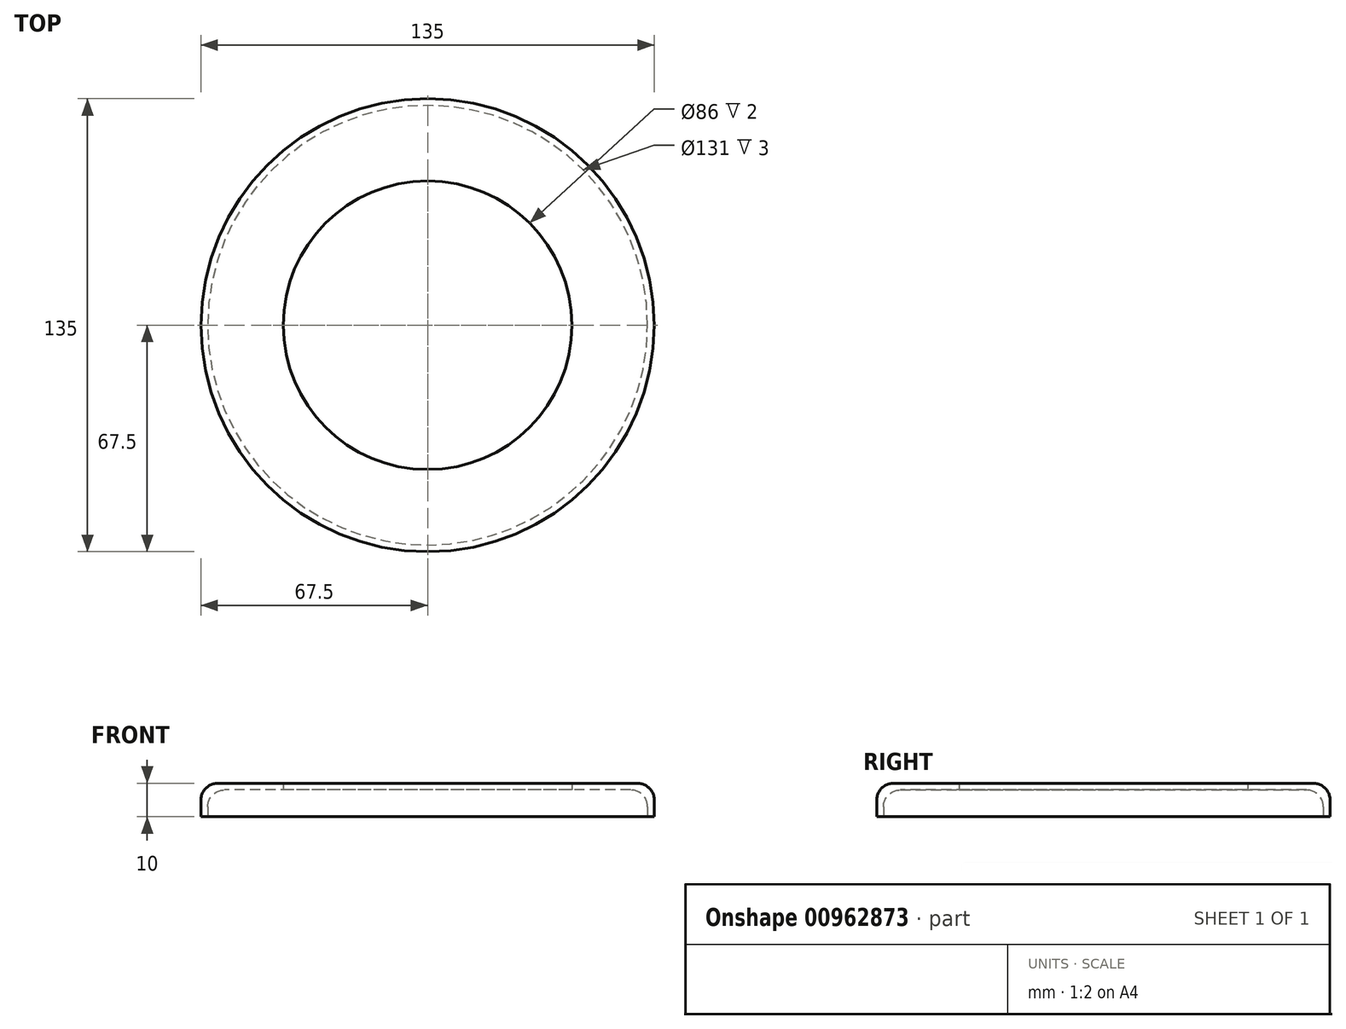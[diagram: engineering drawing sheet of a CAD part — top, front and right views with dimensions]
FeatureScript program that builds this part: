
annotation { "Feature Type Name" : "Feature", "Feature Type Description" : "" }
export const myFeature = defineFeature(function(context is Context, id is Id, definition is map)
    precondition{}
    {
        {
            var Q0;
            Q0=qCreatedBy(makeId("Top.planeOp"),FACE);
            var Q1;
            Q1=qCreatedBy(makeId("Top.planeOp"),FACE);
            var Q2;
            Q2=qCreatedBy(makeId("Top.planeOp"),FACE);
            var sketch = newSketch(context, id + "F0", { "sketchPlane" : qUnion([Q0, Q1, Q2])});
            skCircle(sketch, "E0", {"center": v(0, 0) * mm, "radius": 43 * mm});
            skCircle(sketch, "E1", {"center": v(0, 0) * mm, "radius": 67.5 * mm});
            skCircle(sketch, "E2.0", {"center": v(0, 0) * mm, "radius": 65.5 * mm});
            skSolve(sketch);
        }
        {
            var Q0;
            Q0=makeQuery(id+"F0.imprint","IMPRINT",FACE,{"disambiguationData":[TD([[makeQuery(id+"F0.imprint","IMPRINT",EDGE,{"derivedFrom":sQuery(id+"F0.wireOp",EDGE,"E1")}),1.0]])]});
            var Q1;
            Q1=makeQuery(id+"F0.imprint","IMPRINT",FACE,{"disambiguationData":[TD([[makeQuery(id+"F0.imprint","IMPRINT",EDGE,{"derivedFrom":sQuery(id+"F0.wireOp",EDGE,"E0")}),-1.0]])]});
            extrude(context, id + "F1", {"entities" : qUnion([Q0, Q1]), "depth" : 10 * mm, "offsetDistance" : 25 * mm});
        }
        {
            var Q0;
            Q0=makeQuery(id+"F0.imprint","IMPRINT",FACE,{"disambiguationData":[TD([[makeQuery(id+"F0.imprint","IMPRINT",EDGE,{"derivedFrom":sQuery(id+"F0.wireOp",EDGE,"E0")}),-1.0]])]});
            extrude(context, id + "F2", {"entities" : qUnion([Q0]), "operationType" : NewBodyOperationType.REMOVE, "depth" : (10 - 2) * mm, "offsetDistance" : 25 * mm});
        }
        {
            var Q0;
            Q0=makeQuery(id+"F2.boolean.opBoolean","COPY",EDGE,{"derivedFrom":makeQuery(id+"F2.opExtrude","CAP_EDGE",EDGE,{"disambiguationData":[OSD([sQuery(id+"F0.wireOp",EDGE,"E2.0")])],"isStart":false})});
            var Q1;
            Q1=makeQuery(id+"F1.opExtrude","CAP_EDGE",EDGE,{"disambiguationData":[OSD([sQuery(id+"F0.wireOp",EDGE,"E1")])],"isStart":false});
            fillet(context, id + "F3", {"entities" : qUnion([Q0, Q1]), "radius" : 5 * mm, "tangentPropagation" : true, "allowEdgeOverflow" : false});
        }
    });
